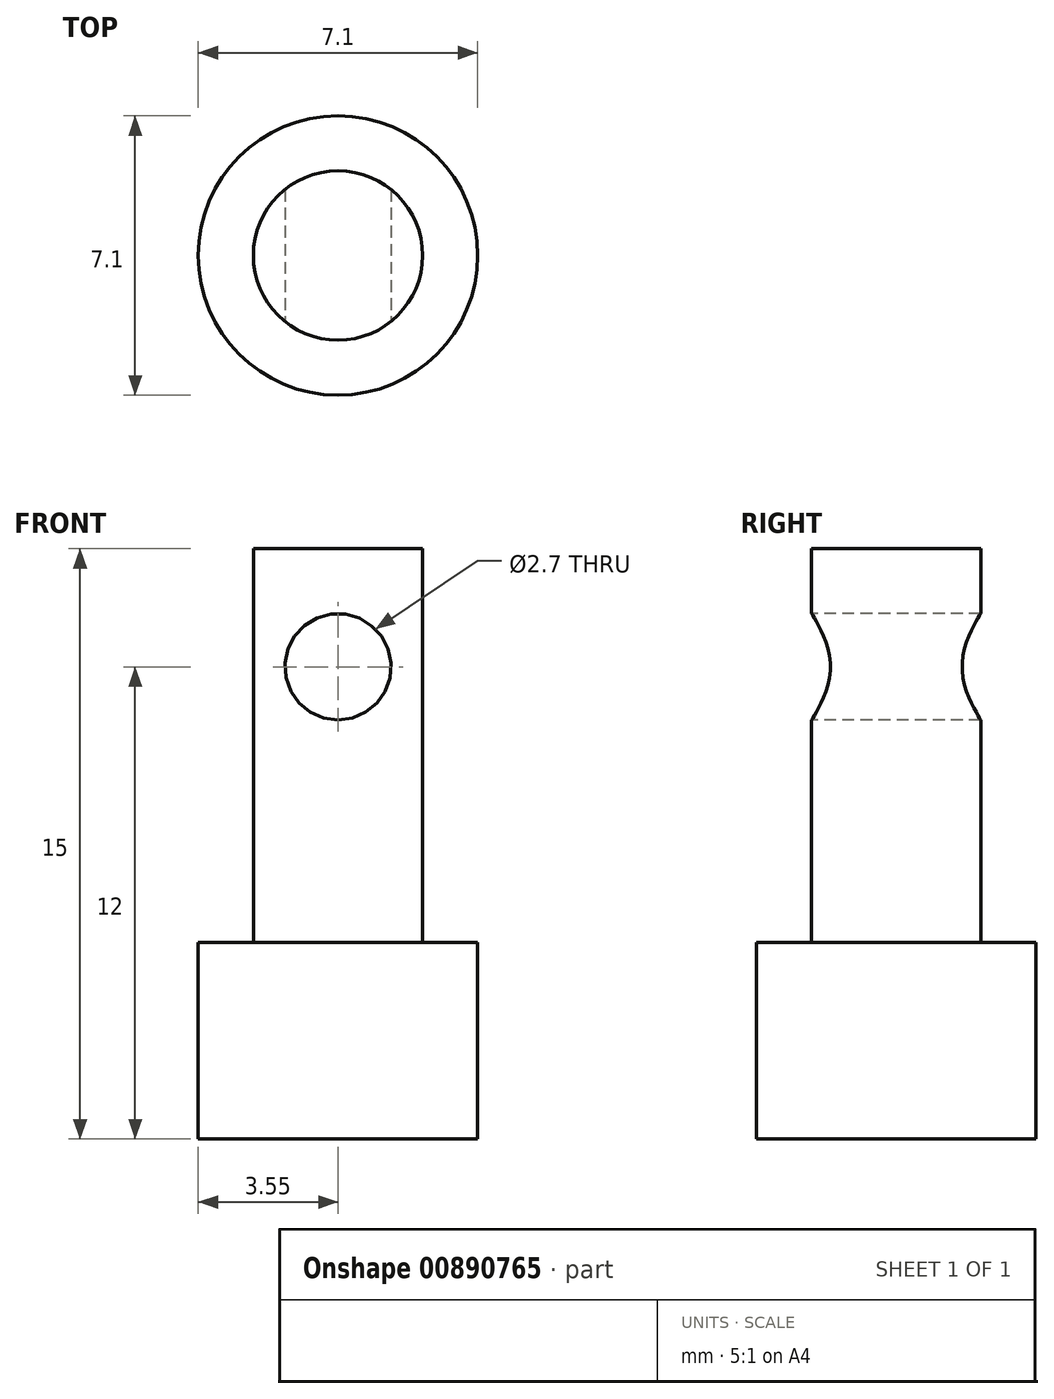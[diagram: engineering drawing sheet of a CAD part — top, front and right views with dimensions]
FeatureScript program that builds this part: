
annotation { "Feature Type Name" : "Feature", "Feature Type Description" : "" }
export const myFeature = defineFeature(function(context is Context, id is Id, definition is map)
    precondition{}
    {
        {
            var Q0;
            Q0=qCreatedBy(makeId("Top.planeOp"),FACE);
            var sketch = newSketch(context, id + "F0", { "sketchPlane" : qUnion([Q0])});
            skCircle(sketch, "E0", {"center": v(0, 0) * mm, "radius": 3.55 * mm});
            skSolve(sketch);
        }
        {
            var Q0;
            Q0=makeQuery(id+"F0.imprint","IMPRINT",FACE,{"disambiguationData":[TD([[makeQuery(id+"F0.imprint","IMPRINT",EDGE,{"derivedFrom":sQuery(id+"F0.wireOp",EDGE,"E0")}),1.0]])]});
            extrude(context, id + "F1", {"entities" : qUnion([Q0]), "depth" : 5 * mm, "offsetDistance" : 25 * mm});
        }
        {
            var Q0;
            Q0=makeQuery(id+"F1.opExtrude","CAP_FACE",FACE,{"disambiguationData":[OSD([sQuery(id+"F0.wireOp",EDGE,"E0")])],"isStart":false});
            var sketch = newSketch(context, id + "F2", { "sketchPlane" : qUnion([Q0])});
            skCircle(sketch, "E1", {"center": v(0, 0) * mm, "radius": 2.15 * mm});
            skSolve(sketch);
        }
        {
            var Q0;
            Q0 = qSketchRegion(id + "F2", true);
            extrude(context, id + "F3", {"entities" : qUnion([Q0]), "operationType" : NewBodyOperationType.ADD, "depth" : 10 * mm, "offsetDistance" : 25 * mm});
        }
        {
            var Q0;
            Q0=qCreatedBy(makeId("Front.planeOp"),FACE);
            var sketch = newSketch(context, id + "F4", { "sketchPlane" : qUnion([Q0])});
            skCircle(sketch, "E2", {"center": v(0, 12) * mm, "radius": 1.35 * mm});
            skSolve(sketch);
        }
        {
            var Q0;
            Q0 = qSketchRegion(id + "F4", true);
            extrude(context, id + "F5", {"entities" : qUnion([Q0]), "operationType" : NewBodyOperationType.REMOVE, "endBound" : BoundingType.UP_TO_NEXT, "oppositeDirection" : true, "depth" : 25 * mm, "offsetDistance" : 25 * mm, "hasSecondDirection" : true, "secondDirectionBound" : SecondDirectionBoundingType.UP_TO_NEXT, "secondDirectionOppositeDirection" : false, "secondDirectionDepth" : 25 * mm});
        }
    });
